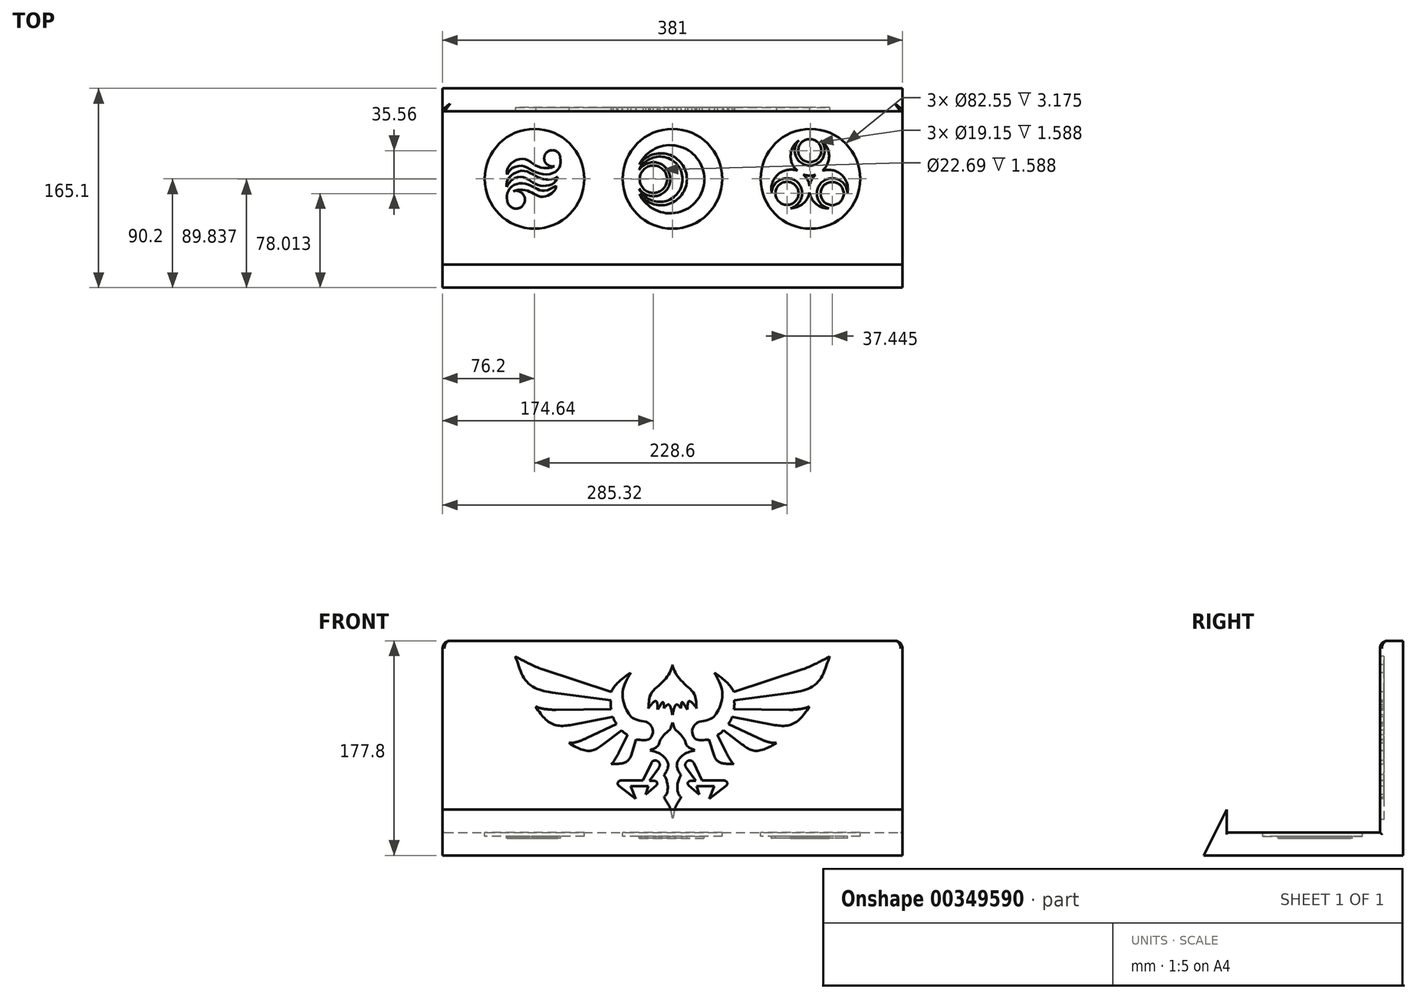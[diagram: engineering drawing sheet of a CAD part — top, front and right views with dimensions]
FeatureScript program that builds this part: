
annotation { "Feature Type Name" : "Feature", "Feature Type Description" : "" }
export const myFeature = defineFeature(function(context is Context, id is Id, definition is map)
    precondition{}
    {
        {
            var Q0;
            Q0=qCreatedBy(makeId("Top.planeOp"),FACE);
            var sketch = newSketch(context, id + "F0", { "sketchPlane" : qUnion([Q0])});
            skLineSegment(sketch, "E0.bottom", {"start": v(-190.5, 63.5) * mm, "end": v(190.5, 63.5) * mm});
            skLineSegment(sketch, "E0.top", {"start": v(-190.5, -63.5) * mm, "end": v(190.5, -63.5) * mm});
            skLineSegment(sketch, "E0.left", {"start": v(-190.5, 63.5) * mm, "end": v(-190.5, -63.5) * mm});
            skLineSegment(sketch, "E0.right", {"start": v(190.5, 63.5) * mm, "end": v(190.5, -63.5) * mm});
            skPoint(sketch, "E0.middle", {"position": v(0, 0) * mm});
            skCircle(sketch, "E1", {"center": v(-114.3, 7.65) * mm, "radius": 41.28 * mm, "construction": true});
            skLineSegment(sketch, "E2", {"start": v(-114.3, 7.65) * mm, "end": v(114.3, 7.65) * mm, "construction": true});
            skLineSegment(sketch, "E3", {"start": v(0, 0) * mm, "end": v(0, 7.65) * mm, "construction": true});
            skCircle(sketch, "E4", {"center": v(0, 7.65) * mm, "radius": 41.28 * mm, "construction": true});
            skCircle(sketch, "E5", {"center": v(114.3, 7.65) * mm, "radius": 41.28 * mm, "construction": true});
            skSolve(sketch);
        }
        {
            var Q0;
            Q0 = qSketchRegion(id + "F0", true);
            extrude(context, id + "F1", {"entities" : qUnion([Q0]), "oppositeDirection" : true, "depth" : 19.05 * mm});
        }
        {
            var Q0;
            Q0=makeQuery(id+"F0.imprint","IMPRINT",FACE,{"disambiguationData":[TD([[makeQuery(id+"F0.imprint","IMPRINT",EDGE,{"derivedFrom":sQuery(id+"F0.wireOp",EDGE,"E0.bottom")}),-1.0]])]});
            var sketch = newSketch(context, id + "F2", { "sketchPlane" : qUnion([Q0])});
            skCircle(sketch, "E6.0", {"center": v(-114.3, 7.65) * mm, "radius": 41.28 * mm});
            skCircle(sketch, "E6.1", {"center": v(0, 7.65) * mm, "radius": 41.28 * mm});
            skCircle(sketch, "E6.2", {"center": v(114.3, 7.65) * mm, "radius": 41.28 * mm});
            skSolve(sketch);
        }
        {
            var Q0;
            Q0 = qSketchRegion(id + "F2", true);
            extrude(context, id + "F3", {"entities" : qUnion([Q0]), "operationType" : NewBodyOperationType.REMOVE, "oppositeDirection" : true, "depth" : 3.17 * mm});
        }
        {
            var Q0;
            Q0=qCreatedBy(makeId("Right.planeOp"),FACE);
            var sketch = newSketch(context, id + "F4", { "sketchPlane" : qUnion([Q0])});
            skLineSegment(sketch, "E7.0", {"start": v(63.5, 0) * mm, "end": v(-63.5, 0) * mm, "construction": true});
            skLineSegment(sketch, "E7.1", {"start": v(63.5, -19.05) * mm, "end": v(-63.5, -19.05) * mm});
            skLineSegment(sketch, "E8", {"start": v(-63.5, -19.05) * mm, "end": v(-82.55, -19.05) * mm});
            skLineSegment(sketch, "E9", {"start": v(-82.55, -19.05) * mm, "end": v(-63.5, 19.05) * mm});
            skLineSegment(sketch, "E10", {"start": v(-63.5, 19.05) * mm, "end": v(-63.5, 0) * mm});
            skLineSegment(sketch, "E11", {"start": v(-63.5, -19.05) * mm, "end": v(-63.5, 0) * mm});
            skLineSegment(sketch, "E12.bottom", {"start": v(63.5, 158.75) * mm, "end": v(82.55, 158.75) * mm});
            skLineSegment(sketch, "E12.top", {"start": v(63.5, -19.05) * mm, "end": v(82.55, -19.05) * mm});
            skLineSegment(sketch, "E12.left", {"start": v(63.5, 158.75) * mm, "end": v(63.5, -19.05) * mm});
            skLineSegment(sketch, "E12.right", {"start": v(82.55, 158.75) * mm, "end": v(82.55, -19.05) * mm});
            skPoint(sketch, "E12.middle", {"position": v(73.03, 69.85) * mm});
            skSolve(sketch);
        }
        {
            var Q0;
            Q0 = qSketchRegion(id + "F4", true);
            var Q1;
            Q1=makeQuery(id+"F1.opExtrude","SWEPT_FACE",FACE,{"disambiguationData":[OSD([sQuery(id+"F0.wireOp",EDGE,"E0.left")])]});
            var Q2;
            Q2=makeQuery(id+"F1.opExtrude","SWEPT_FACE",FACE,{"disambiguationData":[OSD([sQuery(id+"F0.wireOp",EDGE,"E0.right")])]});
            extrude(context, id + "F5", {"entities" : qUnion([Q0]), "operationType" : NewBodyOperationType.ADD, "endBound" : BoundingType.UP_TO_SURFACE, "oppositeDirection" : true, "endBoundEntityFace" : qUnion([Q1]), "depth" : 25.4 * mm, "hasSecondDirection" : true, "secondDirectionBound" : SecondDirectionBoundingType.UP_TO_SURFACE, "secondDirectionOppositeDirection" : false, "secondDirectionBoundEntityFace" : qUnion([Q2]), "secondDirectionDepth" : 25.4 * mm});
        }
        {
            var Q0;
            Q0=makeQuery(id+"F1.opExtrude","CAP_FACE",FACE,{"disambiguationData":[OSD([sQuery(id+"F0.wireOp",EDGE,"E0.bottom"),sQuery(id+"F0.wireOp",EDGE,"E0.top"),sQuery(id+"F0.wireOp",EDGE,"E0.left"),sQuery(id+"F0.wireOp",EDGE,"E0.right")])],"isStart":true});
            var sketch = newSketch(context, id + "F6", { "sketchPlane" : qUnion([Q0])});
            skCircle(sketch, "E13.0", {"center": v(-114.3, 7.65) * mm, "radius": 41.28 * mm, "construction": true});
            skCircle(sketch, "E13.1", {"center": v(0, 7.65) * mm, "radius": 41.28 * mm, "construction": true});
            skCircle(sketch, "E13.2", {"center": v(114.3, 7.65) * mm, "radius": 41.28 * mm, "construction": true});
            skLineSegment(sketch, "E14", {"start": v(114.3, -43.15) * mm, "end": v(114.3, 7.65) * mm, "construction": true});
            skLineSegment(sketch, "E15", {"start": v(0, -43.15) * mm, "end": v(0, 7.65) * mm, "construction": true});
            skLineSegment(sketch, "E16", {"start": v(-114.3, -43.15) * mm, "end": v(-114.3, 7.65) * mm, "construction": true});
            skLineSegment(sketch, "E17", {"start": v(114.3, 7.65) * mm, "end": v(165.1, 7.65) * mm, "construction": true});
            skArc(sketch, "E18", {"start": v(-92.9, 25.2) * mm, "mid": v(-105.08, 28.5) * mm, "end": v(-97.74, 18.23) * mm});
            skFitSpline(sketch, "E19", {"points": [v(-97.74, 18.23) * mm, v(-102.17, 16.72) * mm, v(-112.39, 18.23) * mm, v(-121.9, 23.8) * mm, v(-133.04, 21.02) * mm, v(-136.98, 14.4) * mm, v(-136.98, 11.27) * mm], "startDerivative": vector(-29, -16.65) * mm, "endDerivative": vector(3.25, -26.57) * mm});
            skFitSpline(sketch, "E20", {"points": [v(-136.98, 11.27) * mm, v(-132.58, 16.6) * mm, v(-123.53, 18.23) * mm, v(-116.1, 14.52) * mm, v(-104.96, 11.27) * mm, v(-96.37, 13.94) * mm, v(-92.9, 19.5) * mm, v(-92.9, 25.2) * mm], "startDerivative": vector(25.83, 44.36) * mm, "endDerivative": vector(-2.9, 37.76) * mm});
            skFitSpline(sketch, "E21", {"points": [v(-137.45, 0.94) * mm, v(-133.27, 6.63) * mm, v(-124.69, 9.18) * mm, v(-116.56, 5.12) * mm, v(-109.02, 1.99) * mm, v(-98.8, 3.73) * mm, v(-95.1, 9.18) * mm], "startDerivative": vector(21.44, 40.13) * mm, "endDerivative": vector(17.22, 41.65) * mm});
            skFitSpline(sketch, "E22", {"points": [v(-95.1, 9.18) * mm, v(-99.16, 7.44) * mm, v(-107.05, 7.44) * mm, v(-114.94, 10.8) * mm, v(-123.06, 14.29) * mm, v(-131.18, 12.2) * mm, v(-136.52, 6.98) * mm, v(-137.45, 0.94) * mm], "startDerivative": vector(-32.57, -18.1) * mm, "endDerivative": vector(-0.58, -47.86) * mm});
            skFitSpline(sketch, "E23", {"points": [v(-96.5, 1.93) * mm, v(-105.83, -2.2) * mm, v(-111.44, -1.02) * mm, v(-117.44, 2.07) * mm, v(-125.01, 3.82) * mm, v(-132.77, 1.64) * mm, v(-136.87, -4.62) * mm, v(-136.94, -10.34) * mm], "startDerivative": vector(-33.64, -28.14) * mm, "endDerivative": vector(4.07, -41.96) * mm});
            skFitSpline(sketch, "E24", {"points": [v(-131.9, -2.62) * mm, v(-128.49, -1.5) * mm, v(-121.68, -1.84) * mm, v(-115.23, -4.47) * mm, v(-108.15, -7.25) * mm, v(-100.9, -4.83) * mm, v(-97.36, -1.57) * mm, v(-96.5, 1.93) * mm], "startDerivative": vector(29.28, 16.38) * mm, "endDerivative": vector(0.36, 32.36) * mm});
            skArc(sketch, "E25", {"start": v(-136.94, -10.34) * mm, "mid": v(-123.4, -13.66) * mm, "end": v(-131.9, -2.62) * mm});
            skCircle(sketch, "E26", {"center": v(-15.86, 7.29) * mm, "radius": 11.34 * mm});
            skArc(sketch, "E27", {"start": v(-27.58, -0.5) * mm, "mid": v(-1.8, 7.34) * mm, "end": v(-27.64, 14.98) * mm});
            skArc(sketch, "E28", {"start": v(-27.43, -4.85) * mm, "mid": v(11.88, 7.29) * mm, "end": v(-27.43, 19.42) * mm});
            skArc(sketch, "E29", {"start": v(-27.43, -4.85) * mm, "mid": v(26.3, 7.29) * mm, "end": v(-27.43, 19.42) * mm});
            skCircle(sketch, "E30", {"center": v(94.82, -4.38) * mm, "radius": 9.58 * mm});
            skArc(sketch, "E31", {"start": v(113.5, 1.74) * mm, "mid": v(111.73, 6.97) * mm, "end": v(108.26, 11.27) * mm});
            skLineSegment(sketch, "E32", {"start": v(94.82, -4.38) * mm, "end": v(114.3, 7.65) * mm, "construction": true});
            skCircle(sketch, "E33", {"center": v(113.7, 31.02) * mm, "radius": 9.58 * mm});
            skCircle(sketch, "E34", {"center": v(132.27, -4.54) * mm, "radius": 9.58 * mm});
            skArc(sketch, "E35", {"start": v(104.61, 39.48) * mm, "mid": v(97.86, 27.15) * mm, "end": v(103.44, 14.25) * mm});
            skArc(sketch, "E36", {"start": v(104.61, 39.48) * mm, "mid": v(113.7, 18.6) * mm, "end": v(122.78, 39.48) * mm});
            skArc(sketch, "E37", {"start": v(123.99, 14.25) * mm, "mid": v(129.66, 27.17) * mm, "end": v(122.78, 39.48) * mm});
            skArc(sketch, "E38", {"start": v(108.26, 11.27) * mm, "mid": v(113.37, 10.28) * mm, "end": v(118.54, 10.96) * mm});
            skArc(sketch, "E39", {"start": v(118.54, 10.96) * mm, "mid": v(115.24, 6.78) * mm, "end": v(113.5, 1.74) * mm});
            skArc(sketch, "E40", {"start": v(97.72, -16.62) * mm, "mid": v(107.9, -13.05) * mm, "end": v(113.48, -3.81) * mm});
            skArc(sketch, "E41", {"start": v(113.48, -3.81) * mm, "mid": v(119.07, -13.25) * mm, "end": v(129.42, -16.88) * mm});
            skArc(sketch, "E42", {"start": v(144.92, -3.96) * mm, "mid": v(139.73, 11.21) * mm, "end": v(123.99, 14.25) * mm});
            skArc(sketch, "E43", {"start": v(144.92, -3.96) * mm, "mid": v(124.15, 5.2) * mm, "end": v(129.42, -16.88) * mm});
            skArc(sketch, "E44", {"start": v(97.72, -16.62) * mm, "mid": v(102.79, 5.36) * mm, "end": v(82.24, -3.96) * mm});
            skArc(sketch, "E45", {"start": v(103.44, 14.25) * mm, "mid": v(87.45, 11.42) * mm, "end": v(82.24, -3.96) * mm});
            skArc(sketch, "E46", {"start": v(-27.58, -0.5) * mm, "mid": v(8.3, 7.38) * mm, "end": v(-27.64, 14.98) * mm});
            skSolve(sketch);
        }
        {
            var Q0;
            Q0 = qSketchRegion(id + "F6", true);
            extrude(context, id + "F7", {"entities" : qUnion([Q0]), "operationType" : NewBodyOperationType.REMOVE, "oppositeDirection" : true, "depth" : 4.76 * mm});
        }
        {
            var Q0;
            Q0=makeQuery(id+"F5.opExtrude","SWEPT_FACE",FACE,{"disambiguationData":[OSD([sQuery(id+"F4.wireOp",EDGE,"E12.left")])]});
            var sketch = newSketch(context, id + "F8", { "sketchPlane" : qUnion([Q0])});
            skLineSegment(sketch, "E47", {"start": v(0, 146.55) * mm, "end": v(0, 0) * mm, "construction": true});
            skPoint(sketch, "E47.endSnap0", {"position": v(0, 6.85) * mm});
            skFitSpline(sketch, "E48", {"points": [v(0, 138.8) * mm, v(-6.33, 126.6) * mm, v(-17.94, 114.54) * mm, v(-19.9, 102.9) * mm], "startDerivative": vector(-7.74, -36.83) * mm, "endDerivative": vector(-4.63, -43.03) * mm});
            skFitSpline(sketch, "E49", {"points": [v(-19.9, 102.9) * mm, v(-15.17, 108.29) * mm, v(-13.33, 108.54) * mm, v(-12.25, 101.95) * mm], "startDerivative": vector(11.45, 17.35) * mm, "endDerivative": vector(0.49, -19) * mm});
            skFitSpline(sketch, "E50", {"points": [v(-12.25, 101.95) * mm, v(-8, 107.98) * mm, v(-7, 102.79) * mm], "startDerivative": vector(9.83, 12.97) * mm, "endDerivative": vector(0.6, -15.28) * mm});
            skFitSpline(sketch, "E51", {"points": [v(-7, 102.79) * mm, v(-3.25, 105.95) * mm, v(0, 97.4) * mm], "startDerivative": vector(9.53, 12.21) * mm, "endDerivative": vector(4.7, -21.26) * mm});
            skFitSpline(sketch, "E52", {"points": [v(-34.55, 132.33) * mm, v(-41.33, 115.45) * mm, v(-36.5, 98.57) * mm, v(-28.38, 92.88) * mm], "startDerivative": vector(-26.39, -45.61) * mm, "endDerivative": vector(43.38, -12.96) * mm});
            skFitSpline(sketch, "E53", {"points": [v(-34.55, 132.33) * mm, v(-44.04, 125.1) * mm, v(-50.78, 116.44) * mm], "startDerivative": vector(-20.5, -12.89) * mm, "endDerivative": vector(-9.9, -20.91) * mm});
            skFitSpline(sketch, "E54", {"points": [v(-130.15, 145.84) * mm, v(-119.4, 123.5) * mm, v(-99.4, 115.76) * mm], "startDerivative": vector(17.1, -45.27) * mm, "endDerivative": vector(34.94, -4.52) * mm});
            skFitSpline(sketch, "E55", {"points": [v(-113.32, 104.42) * mm, v(-100.3, 90.23) * mm, v(-84.76, 88.92) * mm], "startDerivative": vector(22.83, -37.15) * mm, "endDerivative": vector(35.03, 6.73) * mm});
            skFitSpline(sketch, "E56", {"points": [v(-85.86, 74.13) * mm, v(-68.47, 67.58) * mm, v(-57.57, 72.94) * mm], "startDerivative": vector(34.1, -22.27) * mm, "endDerivative": vector(23.52, 17.75) * mm});
            skFitSpline(sketch, "E57", {"points": [v(-50.78, 56.52) * mm, v(-39.48, 57.88) * mm, v(-34.48, 63.46) * mm], "startDerivative": vector(25.98, 1.74) * mm, "endDerivative": vector(5.06, 16.05) * mm});
            skFitSpline(sketch, "E58", {"points": [v(-113.32, 104.42) * mm, v(-105.02, 102.08) * mm, v(-96.65, 101.57) * mm], "startDerivative": vector(17.52, -9.04) * mm, "endDerivative": vector(15.97, 0.18) * mm});
            skFitSpline(sketch, "E59", {"points": [v(-85.86, 74.13) * mm, v(-77.63, 75.4) * mm, v(-70.73, 78.3) * mm], "startDerivative": vector(21.48, -0.37) * mm, "endDerivative": vector(13.01, 6.17) * mm});
            skFitSpline(sketch, "E60", {"points": [v(-50.78, 56.52) * mm, v(-47.79, 60.16) * mm, v(-44.36, 66.37) * mm], "startDerivative": vector(7.05, 5.8) * mm, "endDerivative": vector(3.6, 7.11) * mm});
            skLineSegment(sketch, "E61", {"start": v(-44.36, 66.37) * mm, "end": v(-37.12, 80.68) * mm});
            skLineSegment(sketch, "E62", {"start": v(-34.48, 63.46) * mm, "end": v(-30.19, 77.07) * mm});
            skLineSegment(sketch, "E63", {"start": v(-57.57, 72.94) * mm, "end": v(-42.1, 84.6) * mm});
            skLineSegment(sketch, "E64", {"start": v(-70.73, 78.3) * mm, "end": v(-46.3, 89.89) * mm});
            skLineSegment(sketch, "E65", {"start": v(-84.76, 88.92) * mm, "end": v(-49.25, 95.74) * mm});
            skLineSegment(sketch, "E66", {"start": v(-96.65, 101.57) * mm, "end": v(-50.77, 102.08) * mm});
            skLineSegment(sketch, "E67", {"start": v(-51, 109.5) * mm, "end": v(-99.4, 115.76) * mm});
            skLineSegment(sketch, "E68", {"start": v(-50.78, 116.44) * mm, "end": v(-107.72, 135.14) * mm});
            skFitSpline(sketch, "E69", {"points": [v(-107.72, 135.14) * mm, v(-123.76, 142.32) * mm, v(-130.15, 145.84) * mm], "startDerivative": vector(-30.2, 9.92) * mm, "endDerivative": vector(-30.62, 18.72) * mm});
            skArc(sketch, "E70", {"start": v(-51, 109.5) * mm, "mid": v(-51.25, 105.78) * mm, "end": v(-50.77, 102.08) * mm});
            skArc(sketch, "E71", {"start": v(-49.25, 95.74) * mm, "mid": v(-48.11, 92.64) * mm, "end": v(-46.3, 89.89) * mm});
            skArc(sketch, "E72", {"start": v(-42.1, 84.6) * mm, "mid": v(-39.87, 82.32) * mm, "end": v(-37.12, 80.68) * mm});
            skFitSpline(sketch, "E73", {"points": [v(-30.19, 77.07) * mm, v(-24.07, 76.44) * mm, v(-18.99, 77.54) * mm, v(-16.2, 83.72) * mm, v(-18.08, 88.69) * mm, v(-21.97, 91.52) * mm, v(-28.38, 92.88) * mm], "startDerivative": vector(32.02, -6.7) * mm, "endDerivative": vector(-19.87, 5.94) * mm});
            skFitSpline(sketch, "E74", {"points": [v(0, 91.15) * mm, v(-2.1, 85.44) * mm, v(-5.74, 82.05) * mm, v(-10.47, 75.5) * mm, v(-12.05, 71.73) * mm, v(-18.36, 67.97) * mm], "startDerivative": vector(-11.3, -35.1) * mm, "endDerivative": vector(-35.13, -15.96) * mm});
            skFitSpline(sketch, "E75", {"points": [v(-18.36, 67.97) * mm, v(-9.76, 64.76) * mm, v(-3.9, 57.72) * mm, v(-4.58, 51.27) * mm, v(-7.03, 47.76) * mm], "startDerivative": vector(31.25, -8.02) * mm, "endDerivative": vector(-13.7, -16.07) * mm});
            skFitSpline(sketch, "E76", {"points": [v(-7.03, 47.76) * mm, v(-4.49, 41.5) * mm, v(-4.38, 33.4) * mm, v(-7.03, 29.01) * mm], "startDerivative": vector(8.74, -17.19) * mm, "endDerivative": vector(-10.77, -13.09) * mm});
            skFitSpline(sketch, "E77", {"points": [v(-7.03, 29.01) * mm, v(-2.31, 20.72) * mm, v(0, 10.56) * mm], "startDerivative": vector(8.32, -17.02) * mm, "endDerivative": vector(5.76, -19.86) * mm});
            skLineSegment(sketch, "E78", {"start": v(-17.63, 57.43) * mm, "end": v(-24.47, 42.9) * mm});
            skLineSegment(sketch, "E79", {"start": v(-24.47, 42.9) * mm, "end": v(-42.92, 42.9) * mm});
            skLineSegment(sketch, "E80", {"start": v(-44.41, 38.58) * mm, "end": v(-30.53, 27.73) * mm});
            skLineSegment(sketch, "E81", {"start": v(-30.53, 27.73) * mm, "end": v(-34.64, 38.29) * mm});
            skLineSegment(sketch, "E82", {"start": v(-34.64, 38.29) * mm, "end": v(-19.98, 38.29) * mm});
            skLineSegment(sketch, "E83", {"start": v(-19.98, 38.29) * mm, "end": v(-22.32, 31.15) * mm});
            skLineSegment(sketch, "E84", {"start": v(-22.32, 31.15) * mm, "end": v(-13.33, 38.97) * mm});
            skLineSegment(sketch, "E85", {"start": v(-14.68, 42.59) * mm, "end": v(-19.2, 42.59) * mm});
            skLineSegment(sketch, "E86", {"start": v(-19.2, 42.59) * mm, "end": v(-11.26, 53.7) * mm});
            skArc(sketch, "E87", {"start": v(-42.92, 42.9) * mm, "mid": v(-45.2, 41.28) * mm, "end": v(-44.41, 38.58) * mm});
            skArc(sketch, "E88", {"start": v(-13.33, 38.97) * mm, "mid": v(-12.75, 41.25) * mm, "end": v(-14.68, 42.59) * mm});
            skArc(sketch, "E89", {"start": v(-11.26, 53.7) * mm, "mid": v(-12.4, 59.05) * mm, "end": v(-17.63, 57.43) * mm});
            skFitSpline(sketch, "E90.MirrorCS", {"points": [v(50.78, 56.52) * mm, v(47.79, 60.16) * mm, v(44.36, 66.37) * mm], "startDerivative": vector(-7.05, 5.8) * mm, "endDerivative": vector(-3.6, 7.11) * mm});
            skLineSegment(sketch, "E91.MirrorCS", {"start": v(14.68, 42.59) * mm, "end": v(19.2, 42.59) * mm});
            skArc(sketch, "E92.MirrorCS", {"start": v(13.33, 38.97) * mm, "mid": v(12.75, 41.25) * mm, "end": v(14.68, 42.59) * mm});
            skFitSpline(sketch, "E93.MirrorCS", {"points": [v(7.03, 47.76) * mm, v(4.49, 41.5) * mm, v(4.38, 33.4) * mm, v(7.03, 29.01) * mm], "startDerivative": vector(-8.74, -17.19) * mm, "endDerivative": vector(10.77, -13.09) * mm});
            skLineSegment(sketch, "E94.MirrorCS", {"start": v(22.32, 31.15) * mm, "end": v(13.33, 38.97) * mm});
            skArc(sketch, "E95.MirrorCS", {"start": v(42.1, 84.6) * mm, "mid": v(39.87, 82.32) * mm, "end": v(37.12, 80.68) * mm});
            skFitSpline(sketch, "E96.MirrorCS", {"points": [v(12.25, 101.95) * mm, v(8, 107.98) * mm, v(7, 102.79) * mm], "startDerivative": vector(-9.83, 12.97) * mm, "endDerivative": vector(-0.6, -15.28) * mm});
            skArc(sketch, "E97.MirrorCS", {"start": v(49.25, 95.74) * mm, "mid": v(48.11, 92.64) * mm, "end": v(46.3, 89.89) * mm});
            skLineSegment(sketch, "E98.MirrorCS", {"start": v(19.2, 42.59) * mm, "end": v(11.26, 53.7) * mm});
            skLineSegment(sketch, "E99.MirrorCS", {"start": v(30.53, 27.73) * mm, "end": v(34.64, 38.29) * mm});
            skFitSpline(sketch, "E100.MirrorCS", {"points": [v(19.9, 102.9) * mm, v(15.17, 108.29) * mm, v(13.33, 108.54) * mm, v(12.25, 101.95) * mm], "startDerivative": vector(-11.45, 17.35) * mm, "endDerivative": vector(-0.49, -19) * mm});
            skFitSpline(sketch, "E101.MirrorCS", {"points": [v(113.32, 104.42) * mm, v(105.02, 102.08) * mm, v(96.65, 101.57) * mm], "startDerivative": vector(-17.52, -9.04) * mm, "endDerivative": vector(-15.97, 0.18) * mm});
            skFitSpline(sketch, "E102.MirrorCS", {"points": [v(85.86, 74.13) * mm, v(77.63, 75.4) * mm, v(70.73, 78.3) * mm], "startDerivative": vector(-21.48, -0.37) * mm, "endDerivative": vector(-13.01, 6.17) * mm});
            skLineSegment(sketch, "E103.MirrorCS", {"start": v(19.98, 38.29) * mm, "end": v(22.32, 31.15) * mm});
            skArc(sketch, "E104.MirrorCS", {"start": v(42.92, 42.9) * mm, "mid": v(45.2, 41.28) * mm, "end": v(44.41, 38.58) * mm});
            skArc(sketch, "E105.MirrorCS", {"start": v(51, 109.5) * mm, "mid": v(51.25, 105.78) * mm, "end": v(50.77, 102.08) * mm});
            skFitSpline(sketch, "E106.MirrorCS", {"points": [v(107.72, 135.14) * mm, v(123.76, 142.32) * mm, v(130.15, 145.84) * mm], "startDerivative": vector(30.2, 9.92) * mm, "endDerivative": vector(30.62, 18.72) * mm});
            skFitSpline(sketch, "E107.MirrorCS", {"points": [v(113.32, 104.42) * mm, v(100.3, 90.23) * mm, v(84.76, 88.92) * mm], "startDerivative": vector(-22.83, -37.15) * mm, "endDerivative": vector(-35.03, 6.73) * mm});
            skArc(sketch, "E108.MirrorCS", {"start": v(11.26, 53.7) * mm, "mid": v(12.4, 59.05) * mm, "end": v(17.63, 57.43) * mm});
            skFitSpline(sketch, "E109.MirrorCS", {"points": [v(0, 91.15) * mm, v(2.1, 85.44) * mm, v(5.74, 82.05) * mm, v(10.47, 75.5) * mm, v(12.05, 71.73) * mm, v(18.36, 67.97) * mm], "startDerivative": vector(11.3, -35.1) * mm, "endDerivative": vector(35.13, -15.96) * mm});
            skLineSegment(sketch, "E110.MirrorCS", {"start": v(34.48, 63.46) * mm, "end": v(30.19, 77.07) * mm});
            skFitSpline(sketch, "E111.MirrorCS", {"points": [v(30.19, 77.07) * mm, v(24.07, 76.44) * mm, v(18.99, 77.54) * mm, v(16.2, 83.72) * mm, v(18.08, 88.69) * mm, v(21.97, 91.52) * mm, v(28.38, 92.88) * mm], "startDerivative": vector(-32.02, -6.7) * mm, "endDerivative": vector(19.87, 5.94) * mm});
            skFitSpline(sketch, "E112.MirrorCS", {"points": [v(18.36, 67.97) * mm, v(9.76, 64.76) * mm, v(3.9, 57.72) * mm, v(4.58, 51.27) * mm, v(7.03, 47.76) * mm], "startDerivative": vector(-31.25, -8.02) * mm, "endDerivative": vector(13.7, -16.07) * mm});
            skFitSpline(sketch, "E113.MirrorCS", {"points": [v(50.78, 56.52) * mm, v(39.48, 57.88) * mm, v(34.48, 63.46) * mm], "startDerivative": vector(-25.98, 1.74) * mm, "endDerivative": vector(-5.06, 16.05) * mm});
            skFitSpline(sketch, "E114.MirrorCS", {"points": [v(85.86, 74.13) * mm, v(68.47, 67.58) * mm, v(57.57, 72.94) * mm], "startDerivative": vector(-34.1, -22.27) * mm, "endDerivative": vector(-23.52, 17.75) * mm});
            skFitSpline(sketch, "E115.MirrorCS", {"points": [v(130.15, 145.84) * mm, v(119.4, 123.5) * mm, v(99.4, 115.76) * mm], "startDerivative": vector(-17.1, -45.27) * mm, "endDerivative": vector(-34.94, -4.52) * mm});
            skFitSpline(sketch, "E116.MirrorCS", {"points": [v(7, 102.79) * mm, v(3.25, 105.95) * mm, v(0, 97.4) * mm], "startDerivative": vector(-9.53, 12.21) * mm, "endDerivative": vector(-4.7, -21.26) * mm});
            skFitSpline(sketch, "E117.MirrorCS", {"points": [v(34.55, 132.33) * mm, v(44.04, 125.1) * mm, v(50.78, 116.44) * mm], "startDerivative": vector(20.5, -12.89) * mm, "endDerivative": vector(9.9, -20.91) * mm});
            skFitSpline(sketch, "E118.MirrorCS", {"points": [v(0, 138.8) * mm, v(6.33, 126.6) * mm, v(17.94, 114.54) * mm, v(19.9, 102.9) * mm], "startDerivative": vector(7.74, -36.83) * mm, "endDerivative": vector(4.63, -43.03) * mm});
            skLineSegment(sketch, "E119.MirrorCS", {"start": v(17.63, 57.43) * mm, "end": v(24.47, 42.9) * mm});
            skLineSegment(sketch, "E120.MirrorCS", {"start": v(51, 109.5) * mm, "end": v(99.4, 115.76) * mm});
            skFitSpline(sketch, "E121.MirrorCS", {"points": [v(34.55, 132.33) * mm, v(41.33, 115.45) * mm, v(36.5, 98.57) * mm, v(28.38, 92.88) * mm], "startDerivative": vector(26.39, -45.61) * mm, "endDerivative": vector(-43.38, -12.96) * mm});
            skLineSegment(sketch, "E122.MirrorCS", {"start": v(44.41, 38.58) * mm, "end": v(30.53, 27.73) * mm});
            skLineSegment(sketch, "E123.MirrorCS", {"start": v(70.73, 78.3) * mm, "end": v(46.3, 89.89) * mm});
            skLineSegment(sketch, "E124.MirrorCS", {"start": v(34.64, 38.29) * mm, "end": v(19.98, 38.29) * mm});
            skLineSegment(sketch, "E125.MirrorCS", {"start": v(84.76, 88.92) * mm, "end": v(49.25, 95.74) * mm});
            skLineSegment(sketch, "E126.MirrorCS", {"start": v(50.78, 116.44) * mm, "end": v(107.72, 135.14) * mm});
            skLineSegment(sketch, "E127.MirrorCS", {"start": v(57.57, 72.94) * mm, "end": v(42.1, 84.6) * mm});
            skLineSegment(sketch, "E128.MirrorCS", {"start": v(96.65, 101.57) * mm, "end": v(50.77, 102.08) * mm});
            skLineSegment(sketch, "E129.MirrorCS", {"start": v(24.47, 42.9) * mm, "end": v(42.92, 42.9) * mm});
            skLineSegment(sketch, "E130.MirrorCS", {"start": v(44.36, 66.37) * mm, "end": v(37.12, 80.68) * mm});
            skFitSpline(sketch, "E131.MirrorCS", {"points": [v(7.03, 29.01) * mm, v(2.31, 20.72) * mm, v(0, 10.56) * mm], "startDerivative": vector(-8.32, -17.02) * mm, "endDerivative": vector(-5.76, -19.86) * mm});
            skSolve(sketch);
        }
        {
            var Q0;
            Q0 = qSketchRegion(id + "F8", true);
            extrude(context, id + "F9", {"entities" : qUnion([Q0]), "operationType" : NewBodyOperationType.REMOVE, "oppositeDirection" : true, "depth" : 3.17 * mm});
        }
        {
            var Q0;
            Q0=makeQuery(id+"F5.opExtrude","TWEAK_EDGE",EDGE,{"derivedFrom":[makeQuery(id+"F4.imprint","IMPRINT",EDGE,{"derivedFrom":sQuery(id+"F4.wireOp",EDGE,"E9")}),makeQuery(id+"F4.imprint","IMPRINT",EDGE,{"derivedFrom":sQuery(id+"F4.wireOp",EDGE,"E10")}),makeQuery(id+"F4.imprint","IMPRINT",EDGE,{"derivedFrom":sQuery(id+"F4.wireOp",EDGE,"E11")})]});
            var Q1;
            Q1=makeQuery(id+"F5.opExtrude","TWEAK_EDGE",EDGE,{"derivedFrom":[makeQuery(id+"F4.imprint","IMPRINT",EDGE,{"derivedFrom":sQuery(id+"F4.wireOp",EDGE,"E8")}),makeQuery(id+"F4.imprint","IMPRINT",EDGE,{"derivedFrom":sQuery(id+"F4.wireOp",EDGE,"E9")})]});
            var Q2;
            Q2=makeQuery(id+"F5.opExtrude","TWEAK_EDGE",EDGE,{"derivedFrom":[makeQuery(id+"F4.imprint","IMPRINT",EDGE,{"derivedFrom":sQuery(id+"F4.wireOp",EDGE,"E12.bottom")}),makeQuery(id+"F4.imprint","IMPRINT",EDGE,{"derivedFrom":sQuery(id+"F4.wireOp",EDGE,"E12.left")})]});
            var Q3;
            Q3=makeQuery(id+"F5.opExtrude","CAP_EDGE",EDGE,{"disambiguationData":[OSD([sQuery(id+"F4.wireOp",EDGE,"E12.left")])],"isStart":false});
            var Q4;
            Q4=makeQuery(id+"F5.opExtrude","CAP_EDGE",EDGE,{"disambiguationData":[OSD([sQuery(id+"F4.wireOp",EDGE,"E12.left")])],"isStart":true});
            var Q5;
            Q5=makeQuery(id+"F1.opExtrude","CAP_EDGE",EDGE,{"disambiguationData":[OSD([sQuery(id+"F0.wireOp",EDGE,"E0.right")])],"isStart":true});
            var Q6;
            Q6=makeQuery(id+"F1.opExtrude","CAP_EDGE",EDGE,{"disambiguationData":[OSD([sQuery(id+"F0.wireOp",EDGE,"E0.left")])],"isStart":true});
            var Q7;
            Q7=makeQuery(id+"F1.opExtrude","CAP_EDGE",EDGE,{"disambiguationData":[OSD([sQuery(id+"F0.wireOp",EDGE,"E0.bottom")])],"isStart":true});
            var Q8;
            Q8=makeQuery(id+"F1.opExtrude","CAP_EDGE",EDGE,{"disambiguationData":[OSD([sQuery(id+"F0.wireOp",EDGE,"E0.top")])],"isStart":true});
            fillet(context, id + "F10", {"entities" : qUnion([Q0, Q1, Q2, Q3, Q4, Q5, Q6, Q7, Q8]), "radius" : 1.59 * mm, "tangentPropagation" : true, "allowEdgeOverflow" : false});
        }
        {
            var Q0;
            Q0=makeQuery(id+"F5.opExtrude","CAP_EDGE",EDGE,{"disambiguationData":[OSD([sQuery(id+"F4.wireOp",EDGE,"E12.bottom")])],"isStart":false});
            var Q1;
            Q1=makeQuery(id+"F5.opExtrude","CAP_EDGE",EDGE,{"disambiguationData":[OSD([sQuery(id+"F4.wireOp",EDGE,"E12.bottom")])],"isStart":true});
            fillet(context, id + "F11", {"entities" : qUnion([Q0, Q1]), "radius" : 6.35 * mm, "tangentPropagation" : true, "allowEdgeOverflow" : false});
        }
    });
